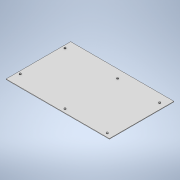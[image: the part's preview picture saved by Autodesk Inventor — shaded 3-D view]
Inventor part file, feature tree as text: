
AUTODESK INVENTOR PART (.ipt)
format: ipt  version: 2021 (Build 250183000, 183)  size: 154,112 bytes
history: native  units: in
note: dims shown in document units (in); Inventor stores cm internally (conversion verified against a paired STEP export)
features: extrude x4, sketch x4
ambient origin geometry x8: Origin, YZ Plane, XZ Plane, XY Plane, X Axis, Y Axis, Z Axis, Center Point
bodies: Solid1 (feature_tree)
feature tree (8):
  extrude  "Extrusion1"  Depth=7.5in
  extrude  "Extrusion2"  Depth=0.063in
  extrude  "Extrusion3"  Depth=3.1in
  extrude  "Extrusion4"  Depth=0.05in
  sketch  "Sketch1"  dims[d0=12.0in d1=7.5in]
  sketch  "Sketch2"  dims[d2=0.063in d3=0.0in d5=0.4in]
  sketch  "Sketch3"  dims[d6=90.0deg d8=3.1in]
  sketch  "Sketch4"  dims[d9=1.8in d10=0.9in d11=6.1in d12=6.1in d13=0.65in d14=11.0in d15=0.2in d16=0.2in d17=0.2in d18=0.2in d19=0.2in d20=0.2in d21=0.0in d22=0.0in d23=0.1in d24=0.0in d25=0.156in d26=0.156in d27=0.156in d28=0.156in d29=0.156in d30=0.05in d31=0.0in d4=0.5in]
